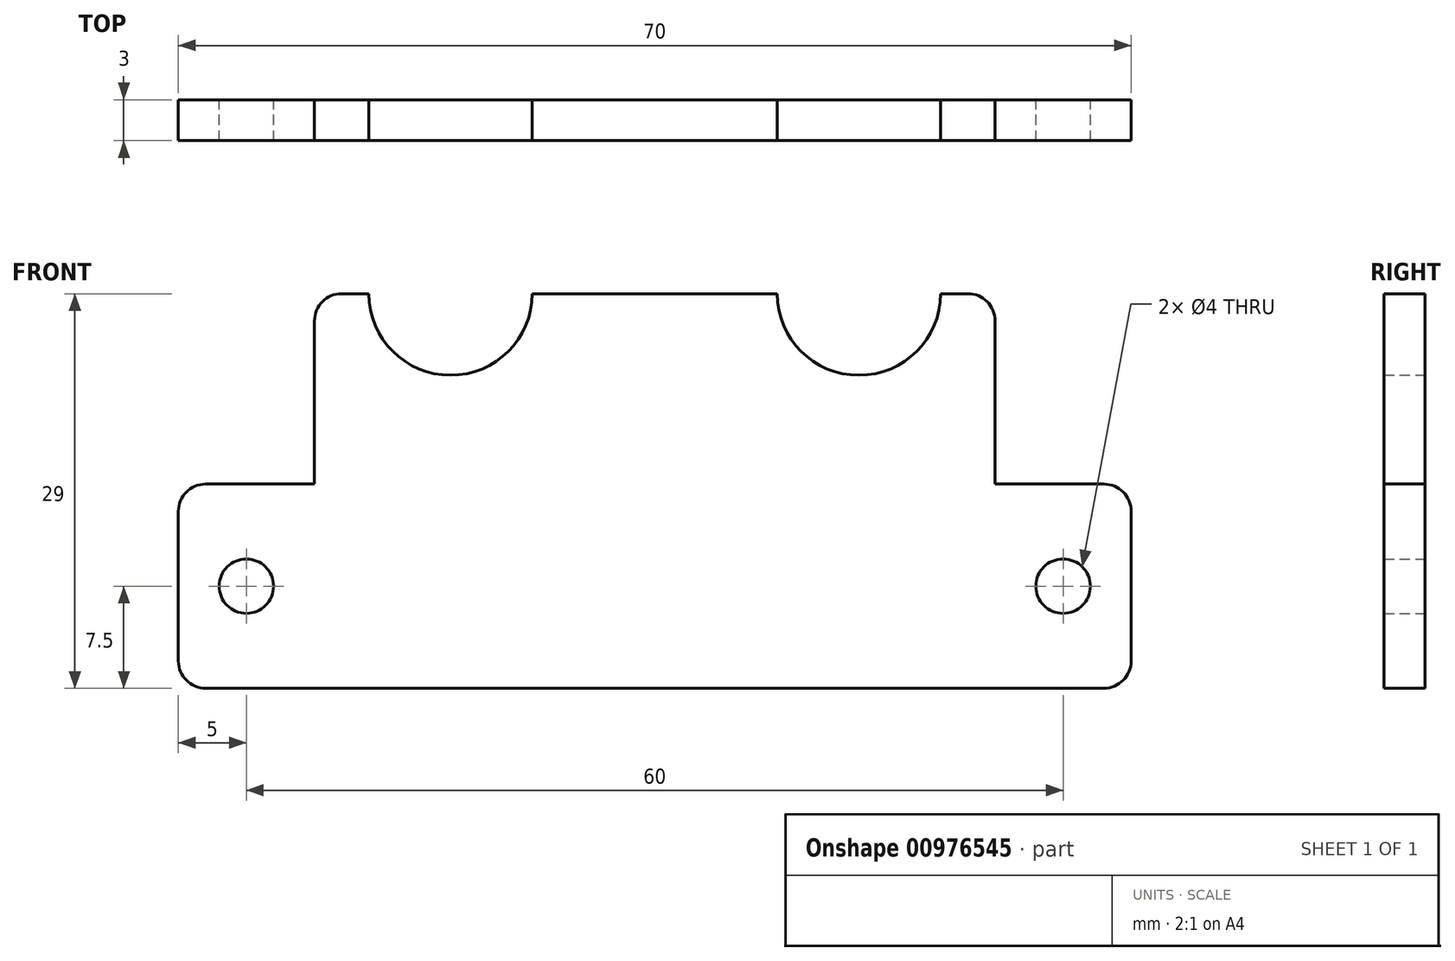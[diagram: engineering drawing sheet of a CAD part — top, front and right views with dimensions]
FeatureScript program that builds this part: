
annotation { "Feature Type Name" : "Feature", "Feature Type Description" : "" }
export const myFeature = defineFeature(function(context is Context, id is Id, definition is map)
    precondition{}
    {
        {
            var Q0;
            Q0=qCreatedBy(makeId("Front.planeOp"),FACE);
            var sketch = newSketch(context, id + "F0", { "sketchPlane" : qUnion([Q0])});
            skLineSegment(sketch, "E0", {"start": v(-35, 0) * mm, "end": v(35, 0) * mm});
            skLineSegment(sketch, "E1", {"start": v(35, 0) * mm, "end": v(35, 15) * mm});
            skLineSegment(sketch, "E2", {"start": v(35, 15) * mm, "end": v(25, 15) * mm});
            skLineSegment(sketch, "E3", {"start": v(25, 15) * mm, "end": v(25, 29) * mm});
            skLineSegment(sketch, "E4", {"start": v(25, 29) * mm, "end": v(-25, 29) * mm});
            skLineSegment(sketch, "E5", {"start": v(-25, 29) * mm, "end": v(-25, 15) * mm});
            skLineSegment(sketch, "E6", {"start": v(-25, 15) * mm, "end": v(-35, 15) * mm});
            skLineSegment(sketch, "E7", {"start": v(-35, 15) * mm, "end": v(-35, 0) * mm});
            skArc(sketch, "E8", {"start": v(-21, 29) * mm, "mid": v(-15, 23) * mm, "end": v(-9, 29) * mm});
            skArc(sketch, "E9.MirrorCS", {"start": v(21, 29) * mm, "mid": v(15, 23) * mm, "end": v(9, 29) * mm});
            skCircle(sketch, "E10", {"center": v(-30, 7.5) * mm, "radius": 2 * mm});
            skPoint(sketch, "E10.centerSnap0", {"position": v(-35, 7.5) * mm});
            skCircle(sketch, "E11", {"center": v(30, 7.5) * mm, "radius": 2 * mm});
            skPoint(sketch, "E11.centerSnap0", {"position": v(35, 7.5) * mm});
            skSolve(sketch);
        }
        {
            var Q0;
            Q0=makeQuery(id+"F0.imprint","IMPRINT",FACE,{"disambiguationData":[TD([[makeQuery(id+"F0.imprint","IMPRINT",EDGE,{"derivedFrom":sQuery(id+"F0.wireOp",EDGE,"E0")}),1.0]])]});
            extrude(context, id + "F1", {"entities" : qUnion([Q0]), "depth" : 3 * mm, "offsetDistance" : 25 * mm});
        }
        {
            var Q0;
            Q0=makeQuery(id+"F1.opExtrude","SWEPT_EDGE",EDGE,{"disambiguationData":[OSD([sQuery(id+"F0.wireOp",EDGE,"E1"),sQuery(id+"F0.wireOp",EDGE,"E2")])]});
            var Q1;
            Q1=makeQuery(id+"F1.opExtrude","SWEPT_EDGE",EDGE,{"disambiguationData":[OSD([sQuery(id+"F0.wireOp",EDGE,"E3"),sQuery(id+"F0.wireOp",EDGE,"E4")])]});
            var Q2;
            Q2=makeQuery(id+"F1.opExtrude","SWEPT_EDGE",EDGE,{"disambiguationData":[OSD([sQuery(id+"F0.wireOp",EDGE,"E0"),sQuery(id+"F0.wireOp",EDGE,"E1")])]});
            var Q3;
            Q3=makeQuery(id+"F1.opExtrude","SWEPT_EDGE",EDGE,{"disambiguationData":[OSD([sQuery(id+"F0.wireOp",EDGE,"E4"),sQuery(id+"F0.wireOp",EDGE,"E5")])]});
            var Q4;
            Q4=makeQuery(id+"F1.opExtrude","SWEPT_EDGE",EDGE,{"disambiguationData":[OSD([sQuery(id+"F0.wireOp",EDGE,"E6"),sQuery(id+"F0.wireOp",EDGE,"E7")])]});
            var Q5;
            Q5=makeQuery(id+"F1.opExtrude","SWEPT_EDGE",EDGE,{"disambiguationData":[OSD([sQuery(id+"F0.wireOp",EDGE,"E0"),sQuery(id+"F0.wireOp",EDGE,"E7")])]});
            fillet(context, id + "F2", {"entities" : qUnion([Q0, Q1, Q2, Q3, Q4, Q5]), "radius" : 2 * mm, "tangentPropagation" : true, "allowEdgeOverflow" : false});
        }
    });
